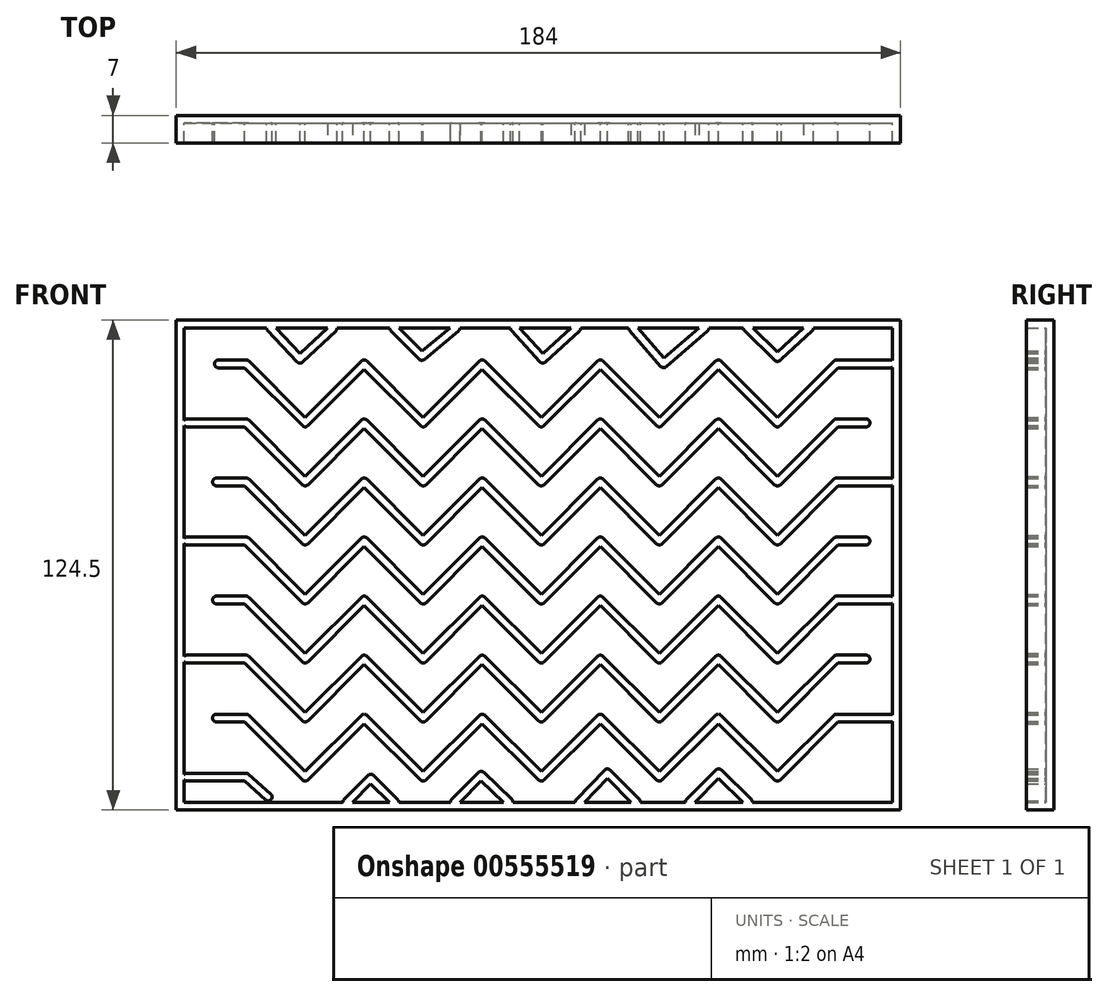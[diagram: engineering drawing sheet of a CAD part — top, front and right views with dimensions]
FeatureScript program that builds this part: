
annotation { "Feature Type Name" : "Feature", "Feature Type Description" : "" }
export const myFeature = defineFeature(function(context is Context, id is Id, definition is map)
    precondition{}
    {
        {
            var Q0;
            Q0=qCreatedBy(makeId("Front.planeOp"),FACE);
            var sketch = newSketch(context, id + "F0", { "sketchPlane" : qUnion([Q0])});
            skLineSegment(sketch, "E0.bottom", {"start": v(-97.27, 65.7) * mm, "end": v(86.73, 65.7) * mm});
            skLineSegment(sketch, "E0.top", {"start": v(-97.27, -58.8) * mm, "end": v(86.73, -58.8) * mm});
            skLineSegment(sketch, "E0.left", {"start": v(-97.27, 65.7) * mm, "end": v(-97.27, -58.8) * mm});
            skLineSegment(sketch, "E0.right", {"start": v(86.73, 65.7) * mm, "end": v(86.73, -58.8) * mm});
            skSolve(sketch);
        }
        {
            var Q0;
            Q0=makeQuery(id+"F0.imprint","IMPRINT",FACE,{"disambiguationData":[TD([[makeQuery(id+"F0.imprint","IMPRINT",EDGE,{"derivedFrom":sQuery(id+"F0.wireOp",EDGE,"E0.bottom")}),-1.0]])]});
            extrude(context, id + "F1", {"entities" : qUnion([Q0]), "depth" : 7 * mm, "offsetDistance" : 25 * mm});
        }
        {
            var Q0;
            Q0=makeQuery(id+"F1.opExtrude","CAP_FACE",FACE,{"disambiguationData":[OSD([sQuery(id+"F0.wireOp",EDGE,"E0.bottom"),sQuery(id+"F0.wireOp",EDGE,"E0.top"),sQuery(id+"F0.wireOp",EDGE,"E0.left"),sQuery(id+"F0.wireOp",EDGE,"E0.right")])],"isStart":false});
            shell(context, id + "F2", {"entities" : qUnion([Q0]), "thickness" : 2 * mm});
        }
        {
            var Q0;
            Q0=makeQuery(id+"F2.opShell","OFFSET_FACE",FACE,{"disambiguationData":[OSD([sQuery(id+"F0.wireOp",EDGE,"E0.bottom"),sQuery(id+"F0.wireOp",EDGE,"E0.top"),sQuery(id+"F0.wireOp",EDGE,"E0.left"),sQuery(id+"F0.wireOp",EDGE,"E0.right")])]});
            var sketch = newSketch(context, id + "F3", { "sketchPlane" : qUnion([Q0])});
            skLineSegment(sketch, "E1", {"start": v(-94.52, 54.57) * mm, "end": v(-94.52, 69.57) * mm, "construction": true});
            skLineSegment(sketch, "E2", {"start": v(-94.52, 39.57) * mm, "end": v(-94.52, 54.57) * mm, "construction": true});
            skLineSegment(sketch, "E3", {"start": v(-94.52, 24.57) * mm, "end": v(-94.52, 39.57) * mm, "construction": true});
            skLineSegment(sketch, "E4", {"start": v(-94.52, 9.57) * mm, "end": v(-94.52, 24.57) * mm, "construction": true});
            skLineSegment(sketch, "E5", {"start": v(-94.52, -5.43) * mm, "end": v(-94.52, 9.57) * mm, "construction": true});
            skLineSegment(sketch, "E6", {"start": v(-94.52, -20.43) * mm, "end": v(-94.52, -5.43) * mm, "construction": true});
            skLineSegment(sketch, "E7", {"start": v(-94.52, -35.43) * mm, "end": v(-94.52, -20.43) * mm, "construction": true});
            skLineSegment(sketch, "E8", {"start": v(-94.52, -50.43) * mm, "end": v(-94.52, -35.43) * mm, "construction": true});
            skLineSegment(sketch, "E9", {"start": v(-94.52, 69.57) * mm, "end": v(111.1, 69.57) * mm, "construction": true});
            skLineSegment(sketch, "E10", {"start": v(-79.52, 54.57) * mm, "end": v(-64.52, 39.57) * mm});
            skLineSegment(sketch, "E11", {"start": v(-64.52, 39.57) * mm, "end": v(-49.52, 54.57) * mm});
            skLineSegment(sketch, "E12", {"start": v(-49.52, 54.57) * mm, "end": v(-34.52, 39.57) * mm});
            skLineSegment(sketch, "E13", {"start": v(-34.52, 39.57) * mm, "end": v(-19.52, 54.57) * mm});
            skLineSegment(sketch, "E14", {"start": v(-19.52, 54.57) * mm, "end": v(-4.52, 39.57) * mm});
            skLineSegment(sketch, "E15", {"start": v(-4.52, 39.57) * mm, "end": v(10.48, 54.57) * mm});
            skLineSegment(sketch, "E16", {"start": v(10.48, 54.57) * mm, "end": v(25.48, 39.57) * mm});
            skLineSegment(sketch, "E17", {"start": v(25.48, 39.57) * mm, "end": v(40.48, 54.57) * mm});
            skLineSegment(sketch, "E18", {"start": v(40.48, 54.57) * mm, "end": v(55.48, 39.57) * mm});
            skLineSegment(sketch, "E19", {"start": v(55.48, 39.57) * mm, "end": v(70.48, 54.57) * mm});
            skLineSegment(sketch, "E20", {"start": v(70.48, 54.57) * mm, "end": v(84.23, 54.57) * mm});
            skLineSegment(sketch, "E21", {"start": v(-79.52, 39.57) * mm, "end": v(-64.52, 24.57) * mm});
            skLineSegment(sketch, "E22", {"start": v(-64.52, 24.57) * mm, "end": v(-49.52, 39.57) * mm});
            skLineSegment(sketch, "E23", {"start": v(-49.52, 39.57) * mm, "end": v(-34.52, 24.57) * mm});
            skLineSegment(sketch, "E24", {"start": v(-34.52, 24.57) * mm, "end": v(-19.52, 39.57) * mm});
            skLineSegment(sketch, "E25", {"start": v(-19.52, 39.57) * mm, "end": v(-4.52, 24.57) * mm});
            skLineSegment(sketch, "E26", {"start": v(-4.52, 24.57) * mm, "end": v(10.48, 39.57) * mm});
            skLineSegment(sketch, "E27", {"start": v(10.48, 39.57) * mm, "end": v(25.48, 24.57) * mm});
            skLineSegment(sketch, "E28", {"start": v(25.48, 24.57) * mm, "end": v(40.48, 39.57) * mm});
            skLineSegment(sketch, "E29", {"start": v(40.48, 39.57) * mm, "end": v(55.48, 24.57) * mm});
            skLineSegment(sketch, "E30", {"start": v(55.48, 24.57) * mm, "end": v(70.48, 39.57) * mm});
            skLineSegment(sketch, "E31", {"start": v(-79.52, 39.57) * mm, "end": v(-94.52, 39.57) * mm});
            skLineSegment(sketch, "E32", {"start": v(-79.52, 24.57) * mm, "end": v(-64.52, 9.57) * mm});
            skLineSegment(sketch, "E33", {"start": v(-64.52, 9.57) * mm, "end": v(-49.52, 24.57) * mm});
            skLineSegment(sketch, "E34", {"start": v(-49.52, 24.57) * mm, "end": v(-34.52, 9.57) * mm});
            skLineSegment(sketch, "E35", {"start": v(-34.52, 9.57) * mm, "end": v(-19.52, 24.57) * mm});
            skLineSegment(sketch, "E36", {"start": v(-19.52, 24.57) * mm, "end": v(-4.52, 9.57) * mm});
            skLineSegment(sketch, "E37", {"start": v(-4.52, 9.57) * mm, "end": v(10.48, 24.57) * mm});
            skLineSegment(sketch, "E38", {"start": v(10.48, 24.57) * mm, "end": v(25.48, 9.57) * mm});
            skLineSegment(sketch, "E39", {"start": v(25.48, 9.57) * mm, "end": v(40.48, 24.57) * mm});
            skLineSegment(sketch, "E40", {"start": v(40.48, 24.57) * mm, "end": v(55.48, 9.57) * mm});
            skLineSegment(sketch, "E41", {"start": v(55.48, 9.57) * mm, "end": v(70.48, 24.57) * mm});
            skLineSegment(sketch, "E42", {"start": v(70.48, 24.57) * mm, "end": v(84.23, 24.57) * mm});
            skLineSegment(sketch, "E43", {"start": v(-79.52, 9.57) * mm, "end": v(-64.52, -5.43) * mm});
            skLineSegment(sketch, "E44", {"start": v(-64.52, -5.43) * mm, "end": v(-49.52, 9.57) * mm});
            skLineSegment(sketch, "E45", {"start": v(-49.52, 9.57) * mm, "end": v(-34.52, -5.43) * mm});
            skLineSegment(sketch, "E46", {"start": v(-34.52, -5.43) * mm, "end": v(-19.52, 9.57) * mm});
            skLineSegment(sketch, "E47", {"start": v(-19.52, 9.57) * mm, "end": v(-4.52, -5.43) * mm});
            skLineSegment(sketch, "E48", {"start": v(-4.52, -5.43) * mm, "end": v(10.48, 9.57) * mm});
            skLineSegment(sketch, "E49", {"start": v(10.48, 9.57) * mm, "end": v(25.48, -5.43) * mm});
            skLineSegment(sketch, "E50", {"start": v(25.48, -5.43) * mm, "end": v(40.48, 9.57) * mm});
            skLineSegment(sketch, "E51", {"start": v(40.48, 9.57) * mm, "end": v(55.48, -5.43) * mm});
            skLineSegment(sketch, "E52", {"start": v(55.48, -5.43) * mm, "end": v(70.48, 9.57) * mm});
            skLineSegment(sketch, "E53", {"start": v(-79.52, 9.57) * mm, "end": v(-94.52, 9.57) * mm});
            skLineSegment(sketch, "E54", {"start": v(-79.52, -5.43) * mm, "end": v(-64.52, -20.43) * mm});
            skLineSegment(sketch, "E55", {"start": v(-64.52, -20.43) * mm, "end": v(-49.52, -5.43) * mm});
            skLineSegment(sketch, "E56", {"start": v(-49.52, -5.43) * mm, "end": v(-34.52, -20.43) * mm});
            skLineSegment(sketch, "E57", {"start": v(-34.52, -20.43) * mm, "end": v(-19.52, -5.43) * mm});
            skLineSegment(sketch, "E58", {"start": v(-19.52, -5.43) * mm, "end": v(-4.52, -20.43) * mm});
            skLineSegment(sketch, "E59", {"start": v(-4.52, -20.43) * mm, "end": v(10.48, -5.43) * mm});
            skLineSegment(sketch, "E60", {"start": v(10.48, -5.43) * mm, "end": v(25.48, -20.43) * mm});
            skLineSegment(sketch, "E61", {"start": v(25.48, -20.43) * mm, "end": v(40.48, -5.43) * mm});
            skLineSegment(sketch, "E62", {"start": v(40.48, -5.43) * mm, "end": v(55.48, -20.43) * mm});
            skLineSegment(sketch, "E63", {"start": v(55.48, -20.43) * mm, "end": v(70.48, -5.43) * mm});
            skLineSegment(sketch, "E64", {"start": v(70.48, -5.43) * mm, "end": v(84.23, -5.43) * mm});
            skLineSegment(sketch, "E65", {"start": v(-79.52, -20.43) * mm, "end": v(-64.52, -35.43) * mm});
            skLineSegment(sketch, "E66", {"start": v(-64.52, -35.43) * mm, "end": v(-49.52, -20.43) * mm});
            skLineSegment(sketch, "E67", {"start": v(-49.52, -20.43) * mm, "end": v(-34.52, -35.43) * mm});
            skLineSegment(sketch, "E68", {"start": v(-34.52, -35.43) * mm, "end": v(-19.52, -20.43) * mm});
            skLineSegment(sketch, "E69", {"start": v(-19.52, -20.43) * mm, "end": v(-4.52, -35.43) * mm});
            skLineSegment(sketch, "E70", {"start": v(-4.52, -35.43) * mm, "end": v(10.48, -20.43) * mm});
            skLineSegment(sketch, "E71", {"start": v(10.48, -20.43) * mm, "end": v(25.48, -35.43) * mm});
            skLineSegment(sketch, "E72", {"start": v(25.48, -35.43) * mm, "end": v(40.48, -20.43) * mm});
            skLineSegment(sketch, "E73", {"start": v(40.48, -20.43) * mm, "end": v(55.48, -35.43) * mm});
            skLineSegment(sketch, "E74", {"start": v(55.48, -35.43) * mm, "end": v(70.48, -20.43) * mm});
            skLineSegment(sketch, "E75", {"start": v(-79.52, -20.43) * mm, "end": v(-94.52, -20.43) * mm});
            skLineSegment(sketch, "E76", {"start": v(-79.52, -35.43) * mm, "end": v(-64.52, -50.43) * mm});
            skLineSegment(sketch, "E77", {"start": v(-64.52, -50.43) * mm, "end": v(-49.52, -35.43) * mm});
            skLineSegment(sketch, "E78", {"start": v(-49.52, -35.43) * mm, "end": v(-34.52, -50.43) * mm});
            skLineSegment(sketch, "E79", {"start": v(-34.52, -50.43) * mm, "end": v(-19.52, -35.43) * mm});
            skLineSegment(sketch, "E80", {"start": v(-19.52, -35.43) * mm, "end": v(-4.52, -50.43) * mm});
            skLineSegment(sketch, "E81", {"start": v(-4.52, -50.43) * mm, "end": v(10.48, -35.43) * mm});
            skLineSegment(sketch, "E82", {"start": v(10.48, -35.43) * mm, "end": v(25.48, -50.43) * mm});
            skLineSegment(sketch, "E83", {"start": v(25.48, -50.43) * mm, "end": v(40.48, -35.43) * mm});
            skLineSegment(sketch, "E84", {"start": v(40.48, -35.43) * mm, "end": v(55.48, -50.43) * mm});
            skLineSegment(sketch, "E85", {"start": v(55.48, -50.43) * mm, "end": v(70.48, -35.43) * mm});
            skLineSegment(sketch, "E86", {"start": v(70.48, -35.43) * mm, "end": v(84.23, -35.43) * mm});
            skLineSegment(sketch, "E87", {"start": v(-79.52, -50.43) * mm, "end": v(-94.52, -50.43) * mm});
            skLineSegment(sketch, "E88", {"start": v(-79.52, -50.43) * mm, "end": v(-73.91, -55.45) * mm});
            skLineSegment(sketch, "E89", {"start": v(-79.52, 54.57) * mm, "end": v(-86.52, 54.57) * mm});
            skLineSegment(sketch, "E90", {"start": v(-79.52, 24.57) * mm, "end": v(-87.02, 24.57) * mm});
            skPoint(sketch, "E90.endSnap0", {"position": v(-87.02, 39.57) * mm});
            skLineSegment(sketch, "E91", {"start": v(-79.52, -5.43) * mm, "end": v(-87.02, -5.43) * mm});
            skPoint(sketch, "E91.endSnap0", {"position": v(-87.02, 9.57) * mm});
            skLineSegment(sketch, "E92", {"start": v(-79.52, -35.43) * mm, "end": v(-87.02, -35.43) * mm});
            skLineSegment(sketch, "E93", {"start": v(70.48, 39.57) * mm, "end": v(77.98, 39.57) * mm});
            skLineSegment(sketch, "E94", {"start": v(70.48, 9.57) * mm, "end": v(77.98, 9.57) * mm});
            skLineSegment(sketch, "E95", {"start": v(70.48, -20.43) * mm, "end": v(77.98, -20.43) * mm});
            skArc(sketch, "E96.0.startCap", {"start": v(-79.52, -49.43) * mm, "mid": v(-78.52, -50.43) * mm, "end": v(-79.52, -51.43) * mm});
            skArc(sketch, "E96.0.endCap", {"start": v(-94.52, -51.43) * mm, "mid": v(-95.52, -50.43) * mm, "end": v(-94.52, -49.43) * mm});
            skLineSegment(sketch, "E96.0.left", {"start": v(-79.52, -51.43) * mm, "end": v(-94.52, -51.43) * mm});
            skLineSegment(sketch, "E96.0.right", {"start": v(-79.52, -49.43) * mm, "end": v(-94.52, -49.43) * mm});
            skArc(sketch, "E96.1.startCap", {"start": v(-50.23, 38.86) * mm, "mid": v(-50.23, 40.28) * mm, "end": v(-48.82, 40.28) * mm});
            skArc(sketch, "E96.1.endCap", {"start": v(-33.82, 25.28) * mm, "mid": v(-33.82, 23.86) * mm, "end": v(-35.23, 23.86) * mm});
            skLineSegment(sketch, "E96.1.left", {"start": v(-48.82, 40.28) * mm, "end": v(-33.82, 25.28) * mm});
            skLineSegment(sketch, "E96.1.right", {"start": v(-50.23, 38.86) * mm, "end": v(-35.23, 23.86) * mm});
            skArc(sketch, "E96.2.startCap", {"start": v(9.77, -21.14) * mm, "mid": v(9.77, -19.72) * mm, "end": v(11.18, -19.72) * mm});
            skArc(sketch, "E96.2.endCap", {"start": v(26.18, -34.72) * mm, "mid": v(26.18, -36.14) * mm, "end": v(24.77, -36.14) * mm});
            skLineSegment(sketch, "E96.2.left", {"start": v(11.18, -19.72) * mm, "end": v(26.18, -34.72) * mm});
            skLineSegment(sketch, "E96.2.right", {"start": v(9.77, -21.14) * mm, "end": v(24.77, -36.14) * mm});
            skArc(sketch, "E96.3.startCap", {"start": v(-63.82, -21.14) * mm, "mid": v(-65.23, -21.14) * mm, "end": v(-65.23, -19.72) * mm});
            skArc(sketch, "E96.3.endCap", {"start": v(-50.23, -4.72) * mm, "mid": v(-48.82, -4.72) * mm, "end": v(-48.82, -6.14) * mm});
            skLineSegment(sketch, "E96.3.left", {"start": v(-65.23, -19.72) * mm, "end": v(-50.23, -4.72) * mm});
            skLineSegment(sketch, "E96.3.right", {"start": v(-63.82, -21.14) * mm, "end": v(-48.82, -6.14) * mm});
            skArc(sketch, "E96.4.startCap", {"start": v(26.18, 8.86) * mm, "mid": v(24.77, 8.86) * mm, "end": v(24.77, 10.28) * mm});
            skArc(sketch, "E96.4.endCap", {"start": v(39.77, 25.28) * mm, "mid": v(41.18, 25.28) * mm, "end": v(41.18, 23.86) * mm});
            skLineSegment(sketch, "E96.4.left", {"start": v(24.77, 10.28) * mm, "end": v(39.77, 25.28) * mm});
            skLineSegment(sketch, "E96.4.right", {"start": v(26.18, 8.86) * mm, "end": v(41.18, 23.86) * mm});
            skArc(sketch, "E96.5.startCap", {"start": v(-20.23, -6.14) * mm, "mid": v(-20.23, -4.72) * mm, "end": v(-18.82, -4.72) * mm});
            skArc(sketch, "E96.5.endCap", {"start": v(-3.82, -19.72) * mm, "mid": v(-3.82, -21.14) * mm, "end": v(-5.23, -21.14) * mm});
            skLineSegment(sketch, "E96.5.left", {"start": v(-18.82, -4.72) * mm, "end": v(-3.82, -19.72) * mm});
            skLineSegment(sketch, "E96.5.right", {"start": v(-20.23, -6.14) * mm, "end": v(-5.23, -21.14) * mm});
            skArc(sketch, "E96.6.startCap", {"start": v(-3.82, 23.86) * mm, "mid": v(-5.23, 23.86) * mm, "end": v(-5.23, 25.28) * mm});
            skArc(sketch, "E96.6.endCap", {"start": v(9.77, 40.28) * mm, "mid": v(11.18, 40.28) * mm, "end": v(11.18, 38.86) * mm});
            skLineSegment(sketch, "E96.6.left", {"start": v(-5.23, 25.28) * mm, "end": v(9.77, 40.28) * mm});
            skLineSegment(sketch, "E96.6.right", {"start": v(-3.82, 23.86) * mm, "end": v(11.18, 38.86) * mm});
            skArc(sketch, "E96.7.startCap", {"start": v(70.48, 23.57) * mm, "mid": v(69.48, 24.57) * mm, "end": v(70.48, 25.57) * mm});
            skArc(sketch, "E96.7.endCap", {"start": v(84.23, 25.57) * mm, "mid": v(85.23, 24.57) * mm, "end": v(84.23, 23.57) * mm});
            skLineSegment(sketch, "E96.7.left", {"start": v(70.48, 25.57) * mm, "end": v(84.23, 25.57) * mm});
            skLineSegment(sketch, "E96.7.right", {"start": v(70.48, 23.57) * mm, "end": v(84.23, 23.57) * mm});
            skArc(sketch, "E96.8.startCap", {"start": v(-79.52, 25.57) * mm, "mid": v(-78.52, 24.57) * mm, "end": v(-79.52, 23.57) * mm});
            skArc(sketch, "E96.8.endCap", {"start": v(-87.02, 23.57) * mm, "mid": v(-88.02, 24.57) * mm, "end": v(-87.02, 25.57) * mm});
            skLineSegment(sketch, "E96.8.left", {"start": v(-79.52, 23.57) * mm, "end": v(-87.02, 23.57) * mm});
            skLineSegment(sketch, "E96.8.right", {"start": v(-79.52, 25.57) * mm, "end": v(-87.02, 25.57) * mm});
            skArc(sketch, "E96.9.startCap", {"start": v(39.77, 23.86) * mm, "mid": v(39.77, 25.28) * mm, "end": v(41.18, 25.28) * mm});
            skArc(sketch, "E96.9.endCap", {"start": v(56.18, 10.28) * mm, "mid": v(56.18, 8.86) * mm, "end": v(54.77, 8.86) * mm});
            skLineSegment(sketch, "E96.9.left", {"start": v(41.18, 25.28) * mm, "end": v(56.18, 10.28) * mm});
            skLineSegment(sketch, "E96.9.right", {"start": v(39.77, 23.86) * mm, "end": v(54.77, 8.86) * mm});
            skArc(sketch, "E96.10.startCap", {"start": v(-50.23, -6.14) * mm, "mid": v(-50.23, -4.72) * mm, "end": v(-48.82, -4.72) * mm});
            skArc(sketch, "E96.10.endCap", {"start": v(-33.82, -19.72) * mm, "mid": v(-33.82, -21.14) * mm, "end": v(-35.23, -21.14) * mm});
            skLineSegment(sketch, "E96.10.left", {"start": v(-48.82, -4.72) * mm, "end": v(-33.82, -19.72) * mm});
            skLineSegment(sketch, "E96.10.right", {"start": v(-50.23, -6.14) * mm, "end": v(-35.23, -21.14) * mm});
            skArc(sketch, "E96.11.startCap", {"start": v(-33.82, 23.86) * mm, "mid": v(-35.23, 23.86) * mm, "end": v(-35.23, 25.28) * mm});
            skArc(sketch, "E96.11.endCap", {"start": v(-20.23, 40.28) * mm, "mid": v(-18.82, 40.28) * mm, "end": v(-18.82, 38.86) * mm});
            skLineSegment(sketch, "E96.11.left", {"start": v(-35.23, 25.28) * mm, "end": v(-20.23, 40.28) * mm});
            skLineSegment(sketch, "E96.11.right", {"start": v(-33.82, 23.86) * mm, "end": v(-18.82, 38.86) * mm});
            skArc(sketch, "E96.12.startCap", {"start": v(-80.19, -51.17) * mm, "mid": v(-80.27, -49.76) * mm, "end": v(-78.86, -49.68) * mm});
            skArc(sketch, "E96.12.endCap", {"start": v(-73.25, -54.7) * mm, "mid": v(-73.17, -56.12) * mm, "end": v(-74.58, -56.2) * mm});
            skLineSegment(sketch, "E96.12.left", {"start": v(-78.86, -49.68) * mm, "end": v(-73.25, -54.7) * mm});
            skLineSegment(sketch, "E96.12.right", {"start": v(-80.19, -51.17) * mm, "end": v(-74.58, -56.2) * mm});
            skArc(sketch, "E96.13.startCap", {"start": v(26.18, -36.14) * mm, "mid": v(24.77, -36.14) * mm, "end": v(24.77, -34.72) * mm});
            skArc(sketch, "E96.13.endCap", {"start": v(39.77, -19.72) * mm, "mid": v(41.18, -19.72) * mm, "end": v(41.18, -21.14) * mm});
            skLineSegment(sketch, "E96.13.left", {"start": v(24.77, -34.72) * mm, "end": v(39.77, -19.72) * mm});
            skLineSegment(sketch, "E96.13.right", {"start": v(26.18, -36.14) * mm, "end": v(41.18, -21.14) * mm});
            skArc(sketch, "E96.14.startCap", {"start": v(-20.23, 53.86) * mm, "mid": v(-20.23, 55.28) * mm, "end": v(-18.82, 55.28) * mm});
            skArc(sketch, "E96.14.endCap", {"start": v(-3.82, 40.28) * mm, "mid": v(-3.82, 38.86) * mm, "end": v(-5.23, 38.86) * mm});
            skLineSegment(sketch, "E96.14.left", {"start": v(-18.82, 55.28) * mm, "end": v(-3.82, 40.28) * mm});
            skLineSegment(sketch, "E96.14.right", {"start": v(-20.23, 53.86) * mm, "end": v(-5.23, 38.86) * mm});
            skArc(sketch, "E96.15.startCap", {"start": v(39.77, 53.86) * mm, "mid": v(39.77, 55.28) * mm, "end": v(41.18, 55.28) * mm});
            skArc(sketch, "E96.15.endCap", {"start": v(56.18, 40.28) * mm, "mid": v(56.18, 38.86) * mm, "end": v(54.77, 38.86) * mm});
            skLineSegment(sketch, "E96.15.left", {"start": v(41.18, 55.28) * mm, "end": v(56.18, 40.28) * mm});
            skLineSegment(sketch, "E96.15.right", {"start": v(39.77, 53.86) * mm, "end": v(54.77, 38.86) * mm});
            skArc(sketch, "E96.16.startCap", {"start": v(-80.23, 53.86) * mm, "mid": v(-80.23, 55.28) * mm, "end": v(-78.82, 55.28) * mm});
            skArc(sketch, "E96.16.endCap", {"start": v(-63.82, 40.28) * mm, "mid": v(-63.82, 38.86) * mm, "end": v(-65.23, 38.86) * mm});
            skLineSegment(sketch, "E96.16.left", {"start": v(-78.82, 55.28) * mm, "end": v(-63.82, 40.28) * mm});
            skLineSegment(sketch, "E96.16.right", {"start": v(-80.23, 53.86) * mm, "end": v(-65.23, 38.86) * mm});
            skArc(sketch, "E96.17.startCap", {"start": v(56.18, -36.14) * mm, "mid": v(54.77, -36.14) * mm, "end": v(54.77, -34.72) * mm});
            skArc(sketch, "E96.17.endCap", {"start": v(69.77, -19.72) * mm, "mid": v(71.18, -19.72) * mm, "end": v(71.18, -21.14) * mm});
            skLineSegment(sketch, "E96.17.left", {"start": v(54.77, -34.72) * mm, "end": v(69.77, -19.72) * mm});
            skLineSegment(sketch, "E96.17.right", {"start": v(56.18, -36.14) * mm, "end": v(71.18, -21.14) * mm});
            skArc(sketch, "E96.18.startCap", {"start": v(56.18, -51.14) * mm, "mid": v(54.77, -51.14) * mm, "end": v(54.77, -49.72) * mm});
            skArc(sketch, "E96.18.endCap", {"start": v(69.77, -34.72) * mm, "mid": v(71.18, -34.72) * mm, "end": v(71.18, -36.14) * mm});
            skLineSegment(sketch, "E96.18.left", {"start": v(54.77, -49.72) * mm, "end": v(69.77, -34.72) * mm});
            skLineSegment(sketch, "E96.18.right", {"start": v(56.18, -51.14) * mm, "end": v(71.18, -36.14) * mm});
            skArc(sketch, "E96.19.startCap", {"start": v(-80.23, 38.86) * mm, "mid": v(-80.23, 40.28) * mm, "end": v(-78.82, 40.28) * mm});
            skArc(sketch, "E96.19.endCap", {"start": v(-63.82, 25.28) * mm, "mid": v(-63.82, 23.86) * mm, "end": v(-65.23, 23.86) * mm});
            skLineSegment(sketch, "E96.19.left", {"start": v(-78.82, 40.28) * mm, "end": v(-63.82, 25.28) * mm});
            skLineSegment(sketch, "E96.19.right", {"start": v(-80.23, 38.86) * mm, "end": v(-65.23, 23.86) * mm});
            skArc(sketch, "E96.20.startCap", {"start": v(56.18, 38.86) * mm, "mid": v(54.77, 38.86) * mm, "end": v(54.77, 40.28) * mm});
            skArc(sketch, "E96.20.endCap", {"start": v(69.77, 55.28) * mm, "mid": v(71.18, 55.28) * mm, "end": v(71.18, 53.86) * mm});
            skLineSegment(sketch, "E96.20.left", {"start": v(54.77, 40.28) * mm, "end": v(69.77, 55.28) * mm});
            skLineSegment(sketch, "E96.20.right", {"start": v(56.18, 38.86) * mm, "end": v(71.18, 53.86) * mm});
            skArc(sketch, "E96.21.startCap", {"start": v(-63.82, 38.86) * mm, "mid": v(-65.23, 38.86) * mm, "end": v(-65.23, 40.28) * mm});
            skArc(sketch, "E96.21.endCap", {"start": v(-50.23, 55.28) * mm, "mid": v(-48.82, 55.28) * mm, "end": v(-48.82, 53.86) * mm});
            skLineSegment(sketch, "E96.21.left", {"start": v(-65.23, 40.28) * mm, "end": v(-50.23, 55.28) * mm});
            skLineSegment(sketch, "E96.21.right", {"start": v(-63.82, 38.86) * mm, "end": v(-48.82, 53.86) * mm});
            skArc(sketch, "E96.22.startCap", {"start": v(-50.23, 53.86) * mm, "mid": v(-50.23, 55.28) * mm, "end": v(-48.82, 55.28) * mm});
            skArc(sketch, "E96.22.endCap", {"start": v(-33.82, 40.28) * mm, "mid": v(-33.82, 38.86) * mm, "end": v(-35.23, 38.86) * mm});
            skLineSegment(sketch, "E96.22.left", {"start": v(-48.82, 55.28) * mm, "end": v(-33.82, 40.28) * mm});
            skLineSegment(sketch, "E96.22.right", {"start": v(-50.23, 53.86) * mm, "end": v(-35.23, 38.86) * mm});
            skArc(sketch, "E96.23.startCap", {"start": v(9.77, -36.14) * mm, "mid": v(9.77, -34.72) * mm, "end": v(11.18, -34.72) * mm});
            skArc(sketch, "E96.23.endCap", {"start": v(26.18, -49.72) * mm, "mid": v(26.18, -51.14) * mm, "end": v(24.77, -51.14) * mm});
            skLineSegment(sketch, "E96.23.left", {"start": v(11.18, -34.72) * mm, "end": v(26.18, -49.72) * mm});
            skLineSegment(sketch, "E96.23.right", {"start": v(9.77, -36.14) * mm, "end": v(24.77, -51.14) * mm});
            skArc(sketch, "E96.24.startCap", {"start": v(26.18, -6.14) * mm, "mid": v(24.77, -6.14) * mm, "end": v(24.77, -4.72) * mm});
            skArc(sketch, "E96.24.endCap", {"start": v(39.77, 10.28) * mm, "mid": v(41.18, 10.28) * mm, "end": v(41.18, 8.86) * mm});
            skLineSegment(sketch, "E96.24.left", {"start": v(24.77, -4.72) * mm, "end": v(39.77, 10.28) * mm});
            skLineSegment(sketch, "E96.24.right", {"start": v(26.18, -6.14) * mm, "end": v(41.18, 8.86) * mm});
            skArc(sketch, "E96.25.startCap", {"start": v(-3.82, 38.86) * mm, "mid": v(-5.23, 38.86) * mm, "end": v(-5.23, 40.28) * mm});
            skArc(sketch, "E96.25.endCap", {"start": v(9.77, 55.28) * mm, "mid": v(11.18, 55.28) * mm, "end": v(11.18, 53.86) * mm});
            skLineSegment(sketch, "E96.25.left", {"start": v(-5.23, 40.28) * mm, "end": v(9.77, 55.28) * mm});
            skLineSegment(sketch, "E96.25.right", {"start": v(-3.82, 38.86) * mm, "end": v(11.18, 53.86) * mm});
            skArc(sketch, "E96.26.startCap", {"start": v(26.18, -51.14) * mm, "mid": v(24.77, -51.14) * mm, "end": v(24.77, -49.72) * mm});
            skArc(sketch, "E96.26.endCap", {"start": v(39.77, -34.72) * mm, "mid": v(41.18, -34.72) * mm, "end": v(41.18, -36.14) * mm});
            skLineSegment(sketch, "E96.26.left", {"start": v(24.77, -49.72) * mm, "end": v(39.77, -34.72) * mm});
            skLineSegment(sketch, "E96.26.right", {"start": v(26.18, -51.14) * mm, "end": v(41.18, -36.14) * mm});
            skArc(sketch, "E96.27.startCap", {"start": v(9.77, 53.86) * mm, "mid": v(9.77, 55.28) * mm, "end": v(11.18, 55.28) * mm});
            skArc(sketch, "E96.27.endCap", {"start": v(26.18, 40.28) * mm, "mid": v(26.18, 38.86) * mm, "end": v(24.77, 38.86) * mm});
            skLineSegment(sketch, "E96.27.left", {"start": v(11.18, 55.28) * mm, "end": v(26.18, 40.28) * mm});
            skLineSegment(sketch, "E96.27.right", {"start": v(9.77, 53.86) * mm, "end": v(24.77, 38.86) * mm});
            skArc(sketch, "E96.28.startCap", {"start": v(-50.23, -21.14) * mm, "mid": v(-50.23, -19.72) * mm, "end": v(-48.82, -19.72) * mm});
            skArc(sketch, "E96.28.endCap", {"start": v(-33.82, -34.72) * mm, "mid": v(-33.82, -36.14) * mm, "end": v(-35.23, -36.14) * mm});
            skLineSegment(sketch, "E96.28.left", {"start": v(-48.82, -19.72) * mm, "end": v(-33.82, -34.72) * mm});
            skLineSegment(sketch, "E96.28.right", {"start": v(-50.23, -21.14) * mm, "end": v(-35.23, -36.14) * mm});
            skArc(sketch, "E96.29.startCap", {"start": v(39.77, 8.86) * mm, "mid": v(39.77, 10.28) * mm, "end": v(41.18, 10.28) * mm});
            skArc(sketch, "E96.29.endCap", {"start": v(56.18, -4.72) * mm, "mid": v(56.18, -6.14) * mm, "end": v(54.77, -6.14) * mm});
            skLineSegment(sketch, "E96.29.left", {"start": v(41.18, 10.28) * mm, "end": v(56.18, -4.72) * mm});
            skLineSegment(sketch, "E96.29.right", {"start": v(39.77, 8.86) * mm, "end": v(54.77, -6.14) * mm});
            skArc(sketch, "E96.30.startCap", {"start": v(-33.82, 8.86) * mm, "mid": v(-35.23, 8.86) * mm, "end": v(-35.23, 10.28) * mm});
            skArc(sketch, "E96.30.endCap", {"start": v(-20.23, 25.28) * mm, "mid": v(-18.82, 25.28) * mm, "end": v(-18.82, 23.86) * mm});
            skLineSegment(sketch, "E96.30.left", {"start": v(-35.23, 10.28) * mm, "end": v(-20.23, 25.28) * mm});
            skLineSegment(sketch, "E96.30.right", {"start": v(-33.82, 8.86) * mm, "end": v(-18.82, 23.86) * mm});
            skArc(sketch, "E96.31.startCap", {"start": v(-63.82, -36.14) * mm, "mid": v(-65.23, -36.14) * mm, "end": v(-65.23, -34.72) * mm});
            skArc(sketch, "E96.31.endCap", {"start": v(-50.23, -19.72) * mm, "mid": v(-48.82, -19.72) * mm, "end": v(-48.82, -21.14) * mm});
            skLineSegment(sketch, "E96.31.left", {"start": v(-65.23, -34.72) * mm, "end": v(-50.23, -19.72) * mm});
            skLineSegment(sketch, "E96.31.right", {"start": v(-63.82, -36.14) * mm, "end": v(-48.82, -21.14) * mm});
            skArc(sketch, "E96.32.startCap", {"start": v(-3.82, 8.86) * mm, "mid": v(-5.23, 8.86) * mm, "end": v(-5.23, 10.28) * mm});
            skArc(sketch, "E96.32.endCap", {"start": v(9.77, 25.28) * mm, "mid": v(11.18, 25.28) * mm, "end": v(11.18, 23.86) * mm});
            skLineSegment(sketch, "E96.32.left", {"start": v(-5.23, 10.28) * mm, "end": v(9.77, 25.28) * mm});
            skLineSegment(sketch, "E96.32.right", {"start": v(-3.82, 8.86) * mm, "end": v(11.18, 23.86) * mm});
            skArc(sketch, "E96.33.startCap", {"start": v(-79.52, 10.57) * mm, "mid": v(-78.52, 9.57) * mm, "end": v(-79.52, 8.57) * mm});
            skArc(sketch, "E96.33.endCap", {"start": v(-94.52, 8.57) * mm, "mid": v(-95.52, 9.57) * mm, "end": v(-94.52, 10.57) * mm});
            skLineSegment(sketch, "E96.33.left", {"start": v(-79.52, 8.57) * mm, "end": v(-94.52, 8.57) * mm});
            skLineSegment(sketch, "E96.33.right", {"start": v(-79.52, 10.57) * mm, "end": v(-94.52, 10.57) * mm});
            skArc(sketch, "E96.34.startCap", {"start": v(-33.82, 38.86) * mm, "mid": v(-35.23, 38.86) * mm, "end": v(-35.23, 40.28) * mm});
            skArc(sketch, "E96.34.endCap", {"start": v(-20.23, 55.28) * mm, "mid": v(-18.82, 55.28) * mm, "end": v(-18.82, 53.86) * mm});
            skLineSegment(sketch, "E96.34.left", {"start": v(-35.23, 40.28) * mm, "end": v(-20.23, 55.28) * mm});
            skLineSegment(sketch, "E96.34.right", {"start": v(-33.82, 38.86) * mm, "end": v(-18.82, 53.86) * mm});
            skArc(sketch, "E96.35.startCap", {"start": v(70.48, 53.57) * mm, "mid": v(69.48, 54.57) * mm, "end": v(70.48, 55.57) * mm});
            skArc(sketch, "E96.35.endCap", {"start": v(84.23, 55.57) * mm, "mid": v(85.23, 54.57) * mm, "end": v(84.23, 53.57) * mm});
            skLineSegment(sketch, "E96.35.left", {"start": v(70.48, 55.57) * mm, "end": v(84.23, 55.57) * mm});
            skLineSegment(sketch, "E96.35.right", {"start": v(70.48, 53.57) * mm, "end": v(84.23, 53.57) * mm});
            skArc(sketch, "E96.36.startCap", {"start": v(39.77, -36.14) * mm, "mid": v(39.77, -34.72) * mm, "end": v(41.18, -34.72) * mm});
            skArc(sketch, "E96.36.endCap", {"start": v(56.18, -49.72) * mm, "mid": v(56.18, -51.14) * mm, "end": v(54.77, -51.14) * mm});
            skLineSegment(sketch, "E96.36.left", {"start": v(41.18, -34.72) * mm, "end": v(56.18, -49.72) * mm});
            skLineSegment(sketch, "E96.36.right", {"start": v(39.77, -36.14) * mm, "end": v(54.77, -51.14) * mm});
            skArc(sketch, "E96.37.startCap", {"start": v(-50.23, 23.86) * mm, "mid": v(-50.23, 25.28) * mm, "end": v(-48.82, 25.28) * mm});
            skArc(sketch, "E96.37.endCap", {"start": v(-33.82, 10.28) * mm, "mid": v(-33.82, 8.86) * mm, "end": v(-35.23, 8.86) * mm});
            skLineSegment(sketch, "E96.37.left", {"start": v(-48.82, 25.28) * mm, "end": v(-33.82, 10.28) * mm});
            skLineSegment(sketch, "E96.37.right", {"start": v(-50.23, 23.86) * mm, "end": v(-35.23, 8.86) * mm});
            skArc(sketch, "E96.38.startCap", {"start": v(-63.82, 23.86) * mm, "mid": v(-65.23, 23.86) * mm, "end": v(-65.23, 25.28) * mm});
            skArc(sketch, "E96.38.endCap", {"start": v(-50.23, 40.28) * mm, "mid": v(-48.82, 40.28) * mm, "end": v(-48.82, 38.86) * mm});
            skLineSegment(sketch, "E96.38.left", {"start": v(-65.23, 25.28) * mm, "end": v(-50.23, 40.28) * mm});
            skLineSegment(sketch, "E96.38.right", {"start": v(-63.82, 23.86) * mm, "end": v(-48.82, 38.86) * mm});
            skArc(sketch, "E96.39.startCap", {"start": v(70.48, -36.43) * mm, "mid": v(69.48, -35.43) * mm, "end": v(70.48, -34.43) * mm});
            skArc(sketch, "E96.39.endCap", {"start": v(84.23, -34.43) * mm, "mid": v(85.23, -35.43) * mm, "end": v(84.23, -36.43) * mm});
            skLineSegment(sketch, "E96.39.left", {"start": v(70.48, -34.43) * mm, "end": v(84.23, -34.43) * mm});
            skLineSegment(sketch, "E96.39.right", {"start": v(70.48, -36.43) * mm, "end": v(84.23, -36.43) * mm});
            skArc(sketch, "E96.40.startCap", {"start": v(-3.82, -36.14) * mm, "mid": v(-5.23, -36.14) * mm, "end": v(-5.23, -34.72) * mm});
            skArc(sketch, "E96.40.endCap", {"start": v(9.77, -19.72) * mm, "mid": v(11.18, -19.72) * mm, "end": v(11.18, -21.14) * mm});
            skLineSegment(sketch, "E96.40.left", {"start": v(-5.23, -34.72) * mm, "end": v(9.77, -19.72) * mm});
            skLineSegment(sketch, "E96.40.right", {"start": v(-3.82, -36.14) * mm, "end": v(11.18, -21.14) * mm});
            skArc(sketch, "E96.41.startCap", {"start": v(-33.82, -21.14) * mm, "mid": v(-35.23, -21.14) * mm, "end": v(-35.23, -19.72) * mm});
            skArc(sketch, "E96.41.endCap", {"start": v(-20.23, -4.72) * mm, "mid": v(-18.82, -4.72) * mm, "end": v(-18.82, -6.14) * mm});
            skLineSegment(sketch, "E96.41.left", {"start": v(-35.23, -19.72) * mm, "end": v(-20.23, -4.72) * mm});
            skLineSegment(sketch, "E96.41.right", {"start": v(-33.82, -21.14) * mm, "end": v(-18.82, -6.14) * mm});
            skArc(sketch, "E96.42.startCap", {"start": v(-33.82, -36.14) * mm, "mid": v(-35.23, -36.14) * mm, "end": v(-35.23, -34.72) * mm});
            skArc(sketch, "E96.42.endCap", {"start": v(-20.23, -19.72) * mm, "mid": v(-18.82, -19.72) * mm, "end": v(-18.82, -21.14) * mm});
            skLineSegment(sketch, "E96.42.left", {"start": v(-35.23, -34.72) * mm, "end": v(-20.23, -19.72) * mm});
            skLineSegment(sketch, "E96.42.right", {"start": v(-33.82, -36.14) * mm, "end": v(-18.82, -21.14) * mm});
            skArc(sketch, "E96.43.startCap", {"start": v(56.18, -6.14) * mm, "mid": v(54.77, -6.14) * mm, "end": v(54.77, -4.72) * mm});
            skArc(sketch, "E96.43.endCap", {"start": v(69.77, 10.28) * mm, "mid": v(71.18, 10.28) * mm, "end": v(71.18, 8.86) * mm});
            skLineSegment(sketch, "E96.43.left", {"start": v(54.77, -4.72) * mm, "end": v(69.77, 10.28) * mm});
            skLineSegment(sketch, "E96.43.right", {"start": v(56.18, -6.14) * mm, "end": v(71.18, 8.86) * mm});
            skArc(sketch, "E96.44.startCap", {"start": v(56.18, 8.86) * mm, "mid": v(54.77, 8.86) * mm, "end": v(54.77, 10.28) * mm});
            skArc(sketch, "E96.44.endCap", {"start": v(69.77, 25.28) * mm, "mid": v(71.18, 25.28) * mm, "end": v(71.18, 23.86) * mm});
            skLineSegment(sketch, "E96.44.left", {"start": v(54.77, 10.28) * mm, "end": v(69.77, 25.28) * mm});
            skLineSegment(sketch, "E96.44.right", {"start": v(56.18, 8.86) * mm, "end": v(71.18, 23.86) * mm});
            skArc(sketch, "E96.45.startCap", {"start": v(-20.23, 38.86) * mm, "mid": v(-20.23, 40.28) * mm, "end": v(-18.82, 40.28) * mm});
            skArc(sketch, "E96.45.endCap", {"start": v(-3.82, 25.28) * mm, "mid": v(-3.82, 23.86) * mm, "end": v(-5.23, 23.86) * mm});
            skLineSegment(sketch, "E96.45.left", {"start": v(-18.82, 40.28) * mm, "end": v(-3.82, 25.28) * mm});
            skLineSegment(sketch, "E96.45.right", {"start": v(-20.23, 38.86) * mm, "end": v(-5.23, 23.86) * mm});
            skArc(sketch, "E96.46.startCap", {"start": v(-79.52, 55.57) * mm, "mid": v(-78.52, 54.57) * mm, "end": v(-79.52, 53.57) * mm});
            skArc(sketch, "E96.46.endCap", {"start": v(-86.52, 53.57) * mm, "mid": v(-87.52, 54.57) * mm, "end": v(-86.52, 55.57) * mm});
            skLineSegment(sketch, "E96.46.left", {"start": v(-79.52, 53.57) * mm, "end": v(-86.52, 53.57) * mm});
            skLineSegment(sketch, "E96.46.right", {"start": v(-79.52, 55.57) * mm, "end": v(-86.52, 55.57) * mm});
            skArc(sketch, "E96.47.startCap", {"start": v(39.77, -21.14) * mm, "mid": v(39.77, -19.72) * mm, "end": v(41.18, -19.72) * mm});
            skArc(sketch, "E96.47.endCap", {"start": v(56.18, -34.72) * mm, "mid": v(56.18, -36.14) * mm, "end": v(54.77, -36.14) * mm});
            skLineSegment(sketch, "E96.47.left", {"start": v(41.18, -19.72) * mm, "end": v(56.18, -34.72) * mm});
            skLineSegment(sketch, "E96.47.right", {"start": v(39.77, -21.14) * mm, "end": v(54.77, -36.14) * mm});
            skArc(sketch, "E96.48.startCap", {"start": v(-20.23, 23.86) * mm, "mid": v(-20.23, 25.28) * mm, "end": v(-18.82, 25.28) * mm});
            skArc(sketch, "E96.48.endCap", {"start": v(-3.82, 10.28) * mm, "mid": v(-3.82, 8.86) * mm, "end": v(-5.23, 8.86) * mm});
            skLineSegment(sketch, "E96.48.left", {"start": v(-18.82, 25.28) * mm, "end": v(-3.82, 10.28) * mm});
            skLineSegment(sketch, "E96.48.right", {"start": v(-20.23, 23.86) * mm, "end": v(-5.23, 8.86) * mm});
            skArc(sketch, "E96.49.startCap", {"start": v(-80.23, -6.14) * mm, "mid": v(-80.23, -4.72) * mm, "end": v(-78.82, -4.72) * mm});
            skArc(sketch, "E96.49.endCap", {"start": v(-63.82, -19.72) * mm, "mid": v(-63.82, -21.14) * mm, "end": v(-65.23, -21.14) * mm});
            skLineSegment(sketch, "E96.49.left", {"start": v(-78.82, -4.72) * mm, "end": v(-63.82, -19.72) * mm});
            skLineSegment(sketch, "E96.49.right", {"start": v(-80.23, -6.14) * mm, "end": v(-65.23, -21.14) * mm});
            skArc(sketch, "E96.50.startCap", {"start": v(9.77, 23.86) * mm, "mid": v(9.77, 25.28) * mm, "end": v(11.18, 25.28) * mm});
            skArc(sketch, "E96.50.endCap", {"start": v(26.18, 10.28) * mm, "mid": v(26.18, 8.86) * mm, "end": v(24.77, 8.86) * mm});
            skLineSegment(sketch, "E96.50.left", {"start": v(11.18, 25.28) * mm, "end": v(26.18, 10.28) * mm});
            skLineSegment(sketch, "E96.50.right", {"start": v(9.77, 23.86) * mm, "end": v(24.77, 8.86) * mm});
            skArc(sketch, "E96.51.startCap", {"start": v(26.18, 38.86) * mm, "mid": v(24.77, 38.86) * mm, "end": v(24.77, 40.28) * mm});
            skArc(sketch, "E96.51.endCap", {"start": v(39.77, 55.28) * mm, "mid": v(41.18, 55.28) * mm, "end": v(41.18, 53.86) * mm});
            skLineSegment(sketch, "E96.51.left", {"start": v(24.77, 40.28) * mm, "end": v(39.77, 55.28) * mm});
            skLineSegment(sketch, "E96.51.right", {"start": v(26.18, 38.86) * mm, "end": v(41.18, 53.86) * mm});
            skArc(sketch, "E96.52.startCap", {"start": v(-63.82, 8.86) * mm, "mid": v(-65.23, 8.86) * mm, "end": v(-65.23, 10.28) * mm});
            skArc(sketch, "E96.52.endCap", {"start": v(-50.23, 25.28) * mm, "mid": v(-48.82, 25.28) * mm, "end": v(-48.82, 23.86) * mm});
            skLineSegment(sketch, "E96.52.left", {"start": v(-65.23, 10.28) * mm, "end": v(-50.23, 25.28) * mm});
            skLineSegment(sketch, "E96.52.right", {"start": v(-63.82, 8.86) * mm, "end": v(-48.82, 23.86) * mm});
            skArc(sketch, "E96.53.startCap", {"start": v(9.77, 8.86) * mm, "mid": v(9.77, 10.28) * mm, "end": v(11.18, 10.28) * mm});
            skArc(sketch, "E96.53.endCap", {"start": v(26.18, -4.72) * mm, "mid": v(26.18, -6.14) * mm, "end": v(24.77, -6.14) * mm});
            skLineSegment(sketch, "E96.53.left", {"start": v(11.18, 10.28) * mm, "end": v(26.18, -4.72) * mm});
            skLineSegment(sketch, "E96.53.right", {"start": v(9.77, 8.86) * mm, "end": v(24.77, -6.14) * mm});
            skArc(sketch, "E96.54.startCap", {"start": v(-80.23, -21.14) * mm, "mid": v(-80.23, -19.72) * mm, "end": v(-78.82, -19.72) * mm});
            skArc(sketch, "E96.54.endCap", {"start": v(-63.82, -34.72) * mm, "mid": v(-63.82, -36.14) * mm, "end": v(-65.23, -36.14) * mm});
            skLineSegment(sketch, "E96.54.left", {"start": v(-78.82, -19.72) * mm, "end": v(-63.82, -34.72) * mm});
            skLineSegment(sketch, "E96.54.right", {"start": v(-80.23, -21.14) * mm, "end": v(-65.23, -36.14) * mm});
            skArc(sketch, "E96.55.startCap", {"start": v(-3.82, -51.14) * mm, "mid": v(-5.23, -51.14) * mm, "end": v(-5.23, -49.72) * mm});
            skArc(sketch, "E96.55.endCap", {"start": v(9.77, -34.72) * mm, "mid": v(11.18, -34.72) * mm, "end": v(11.18, -36.14) * mm});
            skLineSegment(sketch, "E96.55.left", {"start": v(-5.23, -49.72) * mm, "end": v(9.77, -34.72) * mm});
            skLineSegment(sketch, "E96.55.right", {"start": v(-3.82, -51.14) * mm, "end": v(11.18, -36.14) * mm});
            skArc(sketch, "E96.56.startCap", {"start": v(-80.23, 23.86) * mm, "mid": v(-80.23, 25.28) * mm, "end": v(-78.82, 25.28) * mm});
            skArc(sketch, "E96.56.endCap", {"start": v(-63.82, 10.28) * mm, "mid": v(-63.82, 8.86) * mm, "end": v(-65.23, 8.86) * mm});
            skLineSegment(sketch, "E96.56.left", {"start": v(-78.82, 25.28) * mm, "end": v(-63.82, 10.28) * mm});
            skLineSegment(sketch, "E96.56.right", {"start": v(-80.23, 23.86) * mm, "end": v(-65.23, 8.86) * mm});
            skArc(sketch, "E96.57.startCap", {"start": v(-3.82, -6.14) * mm, "mid": v(-5.23, -6.14) * mm, "end": v(-5.23, -4.72) * mm});
            skArc(sketch, "E96.57.endCap", {"start": v(9.77, 10.28) * mm, "mid": v(11.18, 10.28) * mm, "end": v(11.18, 8.86) * mm});
            skLineSegment(sketch, "E96.57.left", {"start": v(-5.23, -4.72) * mm, "end": v(9.77, 10.28) * mm});
            skLineSegment(sketch, "E96.57.right", {"start": v(-3.82, -6.14) * mm, "end": v(11.18, 8.86) * mm});
            skArc(sketch, "E96.58.startCap", {"start": v(70.48, -6.43) * mm, "mid": v(69.48, -5.43) * mm, "end": v(70.48, -4.43) * mm});
            skArc(sketch, "E96.58.endCap", {"start": v(84.23, -4.43) * mm, "mid": v(85.23, -5.43) * mm, "end": v(84.23, -6.43) * mm});
            skLineSegment(sketch, "E96.58.left", {"start": v(70.48, -4.43) * mm, "end": v(84.23, -4.43) * mm});
            skLineSegment(sketch, "E96.58.right", {"start": v(70.48, -6.43) * mm, "end": v(84.23, -6.43) * mm});
            skArc(sketch, "E96.59.startCap", {"start": v(-20.23, -36.14) * mm, "mid": v(-20.23, -34.72) * mm, "end": v(-18.82, -34.72) * mm});
            skArc(sketch, "E96.59.endCap", {"start": v(-3.82, -49.72) * mm, "mid": v(-3.82, -51.14) * mm, "end": v(-5.23, -51.14) * mm});
            skLineSegment(sketch, "E96.59.left", {"start": v(-18.82, -34.72) * mm, "end": v(-3.82, -49.72) * mm});
            skLineSegment(sketch, "E96.59.right", {"start": v(-20.23, -36.14) * mm, "end": v(-5.23, -51.14) * mm});
            skArc(sketch, "E96.60.startCap", {"start": v(70.48, -21.43) * mm, "mid": v(69.48, -20.43) * mm, "end": v(70.48, -19.43) * mm});
            skArc(sketch, "E96.60.endCap", {"start": v(77.98, -19.43) * mm, "mid": v(78.98, -20.43) * mm, "end": v(77.98, -21.43) * mm});
            skLineSegment(sketch, "E96.60.left", {"start": v(70.48, -19.43) * mm, "end": v(77.98, -19.43) * mm});
            skLineSegment(sketch, "E96.60.right", {"start": v(70.48, -21.43) * mm, "end": v(77.98, -21.43) * mm});
            skArc(sketch, "E96.61.startCap", {"start": v(-79.52, 40.57) * mm, "mid": v(-78.52, 39.57) * mm, "end": v(-79.52, 38.57) * mm});
            skArc(sketch, "E96.61.endCap", {"start": v(-94.52, 38.57) * mm, "mid": v(-95.52, 39.57) * mm, "end": v(-94.52, 40.57) * mm});
            skLineSegment(sketch, "E96.61.left", {"start": v(-79.52, 38.57) * mm, "end": v(-94.52, 38.57) * mm});
            skLineSegment(sketch, "E96.61.right", {"start": v(-79.52, 40.57) * mm, "end": v(-94.52, 40.57) * mm});
            skArc(sketch, "E96.62.startCap", {"start": v(-20.23, 8.86) * mm, "mid": v(-20.23, 10.28) * mm, "end": v(-18.82, 10.28) * mm});
            skArc(sketch, "E96.62.endCap", {"start": v(-3.82, -4.72) * mm, "mid": v(-3.82, -6.14) * mm, "end": v(-5.23, -6.14) * mm});
            skLineSegment(sketch, "E96.62.left", {"start": v(-18.82, 10.28) * mm, "end": v(-3.82, -4.72) * mm});
            skLineSegment(sketch, "E96.62.right", {"start": v(-20.23, 8.86) * mm, "end": v(-5.23, -6.14) * mm});
            skArc(sketch, "E96.63.startCap", {"start": v(56.18, -21.14) * mm, "mid": v(54.77, -21.14) * mm, "end": v(54.77, -19.72) * mm});
            skArc(sketch, "E96.63.endCap", {"start": v(69.77, -4.72) * mm, "mid": v(71.18, -4.72) * mm, "end": v(71.18, -6.14) * mm});
            skLineSegment(sketch, "E96.63.left", {"start": v(54.77, -19.72) * mm, "end": v(69.77, -4.72) * mm});
            skLineSegment(sketch, "E96.63.right", {"start": v(56.18, -21.14) * mm, "end": v(71.18, -6.14) * mm});
            skArc(sketch, "E96.64.startCap", {"start": v(-33.82, -51.14) * mm, "mid": v(-35.23, -51.14) * mm, "end": v(-35.23, -49.72) * mm});
            skArc(sketch, "E96.64.endCap", {"start": v(-20.23, -34.72) * mm, "mid": v(-18.82, -34.72) * mm, "end": v(-18.82, -36.14) * mm});
            skLineSegment(sketch, "E96.64.left", {"start": v(-35.23, -49.72) * mm, "end": v(-20.23, -34.72) * mm});
            skLineSegment(sketch, "E96.64.right", {"start": v(-33.82, -51.14) * mm, "end": v(-18.82, -36.14) * mm});
            skArc(sketch, "E96.65.startCap", {"start": v(-63.82, -51.14) * mm, "mid": v(-65.23, -51.14) * mm, "end": v(-65.23, -49.72) * mm});
            skArc(sketch, "E96.65.endCap", {"start": v(-50.23, -34.72) * mm, "mid": v(-48.82, -34.72) * mm, "end": v(-48.82, -36.14) * mm});
            skLineSegment(sketch, "E96.65.left", {"start": v(-65.23, -49.72) * mm, "end": v(-50.23, -34.72) * mm});
            skLineSegment(sketch, "E96.65.right", {"start": v(-63.82, -51.14) * mm, "end": v(-48.82, -36.14) * mm});
            skArc(sketch, "E96.66.startCap", {"start": v(70.48, 38.57) * mm, "mid": v(69.48, 39.57) * mm, "end": v(70.48, 40.57) * mm});
            skArc(sketch, "E96.66.endCap", {"start": v(77.98, 40.57) * mm, "mid": v(78.98, 39.57) * mm, "end": v(77.98, 38.57) * mm});
            skLineSegment(sketch, "E96.66.left", {"start": v(70.48, 40.57) * mm, "end": v(77.98, 40.57) * mm});
            skLineSegment(sketch, "E96.66.right", {"start": v(70.48, 38.57) * mm, "end": v(77.98, 38.57) * mm});
            skArc(sketch, "E96.67.startCap", {"start": v(39.77, 38.86) * mm, "mid": v(39.77, 40.28) * mm, "end": v(41.18, 40.28) * mm});
            skArc(sketch, "E96.67.endCap", {"start": v(56.18, 25.28) * mm, "mid": v(56.18, 23.86) * mm, "end": v(54.77, 23.86) * mm});
            skLineSegment(sketch, "E96.67.left", {"start": v(41.18, 40.28) * mm, "end": v(56.18, 25.28) * mm});
            skLineSegment(sketch, "E96.67.right", {"start": v(39.77, 38.86) * mm, "end": v(54.77, 23.86) * mm});
            skArc(sketch, "E96.68.startCap", {"start": v(-50.23, 8.86) * mm, "mid": v(-50.23, 10.28) * mm, "end": v(-48.82, 10.28) * mm});
            skArc(sketch, "E96.68.endCap", {"start": v(-33.82, -4.72) * mm, "mid": v(-33.82, -6.14) * mm, "end": v(-35.23, -6.14) * mm});
            skLineSegment(sketch, "E96.68.left", {"start": v(-48.82, 10.28) * mm, "end": v(-33.82, -4.72) * mm});
            skLineSegment(sketch, "E96.68.right", {"start": v(-50.23, 8.86) * mm, "end": v(-35.23, -6.14) * mm});
            skArc(sketch, "E96.69.startCap", {"start": v(26.18, -21.14) * mm, "mid": v(24.77, -21.14) * mm, "end": v(24.77, -19.72) * mm});
            skArc(sketch, "E96.69.endCap", {"start": v(39.77, -4.72) * mm, "mid": v(41.18, -4.72) * mm, "end": v(41.18, -6.14) * mm});
            skLineSegment(sketch, "E96.69.left", {"start": v(24.77, -19.72) * mm, "end": v(39.77, -4.72) * mm});
            skLineSegment(sketch, "E96.69.right", {"start": v(26.18, -21.14) * mm, "end": v(41.18, -6.14) * mm});
            skArc(sketch, "E96.70.startCap", {"start": v(70.48, 8.57) * mm, "mid": v(69.48, 9.57) * mm, "end": v(70.48, 10.57) * mm});
            skArc(sketch, "E96.70.endCap", {"start": v(77.98, 10.57) * mm, "mid": v(78.98, 9.57) * mm, "end": v(77.98, 8.57) * mm});
            skLineSegment(sketch, "E96.70.left", {"start": v(70.48, 10.57) * mm, "end": v(77.98, 10.57) * mm});
            skLineSegment(sketch, "E96.70.right", {"start": v(70.48, 8.57) * mm, "end": v(77.98, 8.57) * mm});
            skArc(sketch, "E96.71.startCap", {"start": v(56.18, 23.86) * mm, "mid": v(54.77, 23.86) * mm, "end": v(54.77, 25.28) * mm});
            skArc(sketch, "E96.71.endCap", {"start": v(69.77, 40.28) * mm, "mid": v(71.18, 40.28) * mm, "end": v(71.18, 38.86) * mm});
            skLineSegment(sketch, "E96.71.left", {"start": v(54.77, 25.28) * mm, "end": v(69.77, 40.28) * mm});
            skLineSegment(sketch, "E96.71.right", {"start": v(56.18, 23.86) * mm, "end": v(71.18, 38.86) * mm});
            skArc(sketch, "E96.72.startCap", {"start": v(-33.82, -6.14) * mm, "mid": v(-35.23, -6.14) * mm, "end": v(-35.23, -4.72) * mm});
            skArc(sketch, "E96.72.endCap", {"start": v(-20.23, 10.28) * mm, "mid": v(-18.82, 10.28) * mm, "end": v(-18.82, 8.86) * mm});
            skLineSegment(sketch, "E96.72.left", {"start": v(-35.23, -4.72) * mm, "end": v(-20.23, 10.28) * mm});
            skLineSegment(sketch, "E96.72.right", {"start": v(-33.82, -6.14) * mm, "end": v(-18.82, 8.86) * mm});
            skArc(sketch, "E96.73.startCap", {"start": v(39.77, -6.14) * mm, "mid": v(39.77, -4.72) * mm, "end": v(41.18, -4.72) * mm});
            skArc(sketch, "E96.73.endCap", {"start": v(56.18, -19.72) * mm, "mid": v(56.18, -21.14) * mm, "end": v(54.77, -21.14) * mm});
            skLineSegment(sketch, "E96.73.left", {"start": v(41.18, -4.72) * mm, "end": v(56.18, -19.72) * mm});
            skLineSegment(sketch, "E96.73.right", {"start": v(39.77, -6.14) * mm, "end": v(54.77, -21.14) * mm});
            skArc(sketch, "E96.74.startCap", {"start": v(-50.23, -36.14) * mm, "mid": v(-50.23, -34.72) * mm, "end": v(-48.82, -34.72) * mm});
            skArc(sketch, "E96.74.endCap", {"start": v(-33.82, -49.72) * mm, "mid": v(-33.82, -51.14) * mm, "end": v(-35.23, -51.14) * mm});
            skLineSegment(sketch, "E96.74.left", {"start": v(-48.82, -34.72) * mm, "end": v(-33.82, -49.72) * mm});
            skLineSegment(sketch, "E96.74.right", {"start": v(-50.23, -36.14) * mm, "end": v(-35.23, -51.14) * mm});
            skArc(sketch, "E96.75.startCap", {"start": v(-80.23, -36.14) * mm, "mid": v(-80.23, -34.72) * mm, "end": v(-78.82, -34.72) * mm});
            skArc(sketch, "E96.75.endCap", {"start": v(-63.82, -49.72) * mm, "mid": v(-63.82, -51.14) * mm, "end": v(-65.23, -51.14) * mm});
            skLineSegment(sketch, "E96.75.left", {"start": v(-78.82, -34.72) * mm, "end": v(-63.82, -49.72) * mm});
            skLineSegment(sketch, "E96.75.right", {"start": v(-80.23, -36.14) * mm, "end": v(-65.23, -51.14) * mm});
            skArc(sketch, "E96.76.startCap", {"start": v(26.18, 23.86) * mm, "mid": v(24.77, 23.86) * mm, "end": v(24.77, 25.28) * mm});
            skArc(sketch, "E96.76.endCap", {"start": v(39.77, 40.28) * mm, "mid": v(41.18, 40.28) * mm, "end": v(41.18, 38.86) * mm});
            skLineSegment(sketch, "E96.76.left", {"start": v(24.77, 25.28) * mm, "end": v(39.77, 40.28) * mm});
            skLineSegment(sketch, "E96.76.right", {"start": v(26.18, 23.86) * mm, "end": v(41.18, 38.86) * mm});
            skArc(sketch, "E96.77.startCap", {"start": v(-79.52, -34.43) * mm, "mid": v(-78.52, -35.43) * mm, "end": v(-79.52, -36.43) * mm});
            skArc(sketch, "E96.77.endCap", {"start": v(-87.02, -36.43) * mm, "mid": v(-88.02, -35.43) * mm, "end": v(-87.02, -34.43) * mm});
            skLineSegment(sketch, "E96.77.left", {"start": v(-79.52, -36.43) * mm, "end": v(-87.02, -36.43) * mm});
            skLineSegment(sketch, "E96.77.right", {"start": v(-79.52, -34.43) * mm, "end": v(-87.02, -34.43) * mm});
            skArc(sketch, "E96.78.startCap", {"start": v(-63.82, -6.14) * mm, "mid": v(-65.23, -6.14) * mm, "end": v(-65.23, -4.72) * mm});
            skArc(sketch, "E96.78.endCap", {"start": v(-50.23, 10.28) * mm, "mid": v(-48.82, 10.28) * mm, "end": v(-48.82, 8.86) * mm});
            skLineSegment(sketch, "E96.78.left", {"start": v(-65.23, -4.72) * mm, "end": v(-50.23, 10.28) * mm});
            skLineSegment(sketch, "E96.78.right", {"start": v(-63.82, -6.14) * mm, "end": v(-48.82, 8.86) * mm});
            skArc(sketch, "E96.79.startCap", {"start": v(9.77, -6.14) * mm, "mid": v(9.77, -4.72) * mm, "end": v(11.18, -4.72) * mm});
            skArc(sketch, "E96.79.endCap", {"start": v(26.18, -19.72) * mm, "mid": v(26.18, -21.14) * mm, "end": v(24.77, -21.14) * mm});
            skLineSegment(sketch, "E96.79.left", {"start": v(11.18, -4.72) * mm, "end": v(26.18, -19.72) * mm});
            skLineSegment(sketch, "E96.79.right", {"start": v(9.77, -6.14) * mm, "end": v(24.77, -21.14) * mm});
            skArc(sketch, "E96.80.startCap", {"start": v(-79.52, -4.43) * mm, "mid": v(-78.52, -5.43) * mm, "end": v(-79.52, -6.43) * mm});
            skArc(sketch, "E96.80.endCap", {"start": v(-87.02, -6.43) * mm, "mid": v(-88.02, -5.43) * mm, "end": v(-87.02, -4.43) * mm});
            skLineSegment(sketch, "E96.80.left", {"start": v(-79.52, -6.43) * mm, "end": v(-87.02, -6.43) * mm});
            skLineSegment(sketch, "E96.80.right", {"start": v(-79.52, -4.43) * mm, "end": v(-87.02, -4.43) * mm});
            skArc(sketch, "E96.81.startCap", {"start": v(-80.23, 8.86) * mm, "mid": v(-80.23, 10.28) * mm, "end": v(-78.82, 10.28) * mm});
            skArc(sketch, "E96.81.endCap", {"start": v(-63.82, -4.72) * mm, "mid": v(-63.82, -6.14) * mm, "end": v(-65.23, -6.14) * mm});
            skLineSegment(sketch, "E96.81.left", {"start": v(-78.82, 10.28) * mm, "end": v(-63.82, -4.72) * mm});
            skLineSegment(sketch, "E96.81.right", {"start": v(-80.23, 8.86) * mm, "end": v(-65.23, -6.14) * mm});
            skArc(sketch, "E96.82.startCap", {"start": v(9.77, 38.86) * mm, "mid": v(9.77, 40.28) * mm, "end": v(11.18, 40.28) * mm});
            skArc(sketch, "E96.82.endCap", {"start": v(26.18, 25.28) * mm, "mid": v(26.18, 23.86) * mm, "end": v(24.77, 23.86) * mm});
            skLineSegment(sketch, "E96.82.left", {"start": v(11.18, 40.28) * mm, "end": v(26.18, 25.28) * mm});
            skLineSegment(sketch, "E96.82.right", {"start": v(9.77, 38.86) * mm, "end": v(24.77, 23.86) * mm});
            skArc(sketch, "E96.83.startCap", {"start": v(-20.23, -21.14) * mm, "mid": v(-20.23, -19.72) * mm, "end": v(-18.82, -19.72) * mm});
            skArc(sketch, "E96.83.endCap", {"start": v(-3.82, -34.72) * mm, "mid": v(-3.82, -36.14) * mm, "end": v(-5.23, -36.14) * mm});
            skLineSegment(sketch, "E96.83.left", {"start": v(-18.82, -19.72) * mm, "end": v(-3.82, -34.72) * mm});
            skLineSegment(sketch, "E96.83.right", {"start": v(-20.23, -21.14) * mm, "end": v(-5.23, -36.14) * mm});
            skArc(sketch, "E96.84.startCap", {"start": v(-3.82, -21.14) * mm, "mid": v(-5.23, -21.14) * mm, "end": v(-5.23, -19.72) * mm});
            skArc(sketch, "E96.84.endCap", {"start": v(9.77, -4.72) * mm, "mid": v(11.18, -4.72) * mm, "end": v(11.18, -6.14) * mm});
            skLineSegment(sketch, "E96.84.left", {"start": v(-5.23, -19.72) * mm, "end": v(9.77, -4.72) * mm});
            skLineSegment(sketch, "E96.84.right", {"start": v(-3.82, -21.14) * mm, "end": v(11.18, -6.14) * mm});
            skArc(sketch, "E96.85.startCap", {"start": v(-79.52, -19.43) * mm, "mid": v(-78.52, -20.43) * mm, "end": v(-79.52, -21.43) * mm});
            skArc(sketch, "E96.85.endCap", {"start": v(-94.52, -21.43) * mm, "mid": v(-95.52, -20.43) * mm, "end": v(-94.52, -19.43) * mm});
            skLineSegment(sketch, "E96.85.left", {"start": v(-79.52, -21.43) * mm, "end": v(-94.52, -21.43) * mm});
            skLineSegment(sketch, "E96.85.right", {"start": v(-79.52, -19.43) * mm, "end": v(-94.52, -19.43) * mm});
            skLineSegment(sketch, "E97", {"start": v(-73.33, 63.7) * mm, "end": v(-65.83, 55.75) * mm});
            skLineSegment(sketch, "E98", {"start": v(-65.83, 55.75) * mm, "end": v(-57.4, 63.7) * mm});
            skLineSegment(sketch, "E99", {"start": v(-42.05, 63.7) * mm, "end": v(-34.9, 56.46) * mm});
            skLineSegment(sketch, "E100", {"start": v(-34.9, 56.46) * mm, "end": v(-26.2, 63.7) * mm});
            skLineSegment(sketch, "E101", {"start": v(-11.4, 63.7) * mm, "end": v(-4.16, 55.77) * mm});
            skLineSegment(sketch, "E102", {"start": v(-4.16, 55.77) * mm, "end": v(4.52, 63.7) * mm});
            skLineSegment(sketch, "E103", {"start": v(18.67, 63.7) * mm, "end": v(26.57, 54.6) * mm});
            skLineSegment(sketch, "E104", {"start": v(26.57, 54.6) * mm, "end": v(37.07, 63.7) * mm});
            skLineSegment(sketch, "E105", {"start": v(47.77, 63.7) * mm, "end": v(55.5, 56.19) * mm});
            skLineSegment(sketch, "E106", {"start": v(55.42, 56.27) * mm, "end": v(63.62, 63.7) * mm});
            skLineSegment(sketch, "E107", {"start": v(-4.16, 55.77) * mm, "end": v(-4.16, 55.77) * mm});
            skArc(sketch, "E108.0.startCap", {"start": v(-3.49, 55.04) * mm, "mid": v(-4.9, 55.1) * mm, "end": v(-4.84, 56.51) * mm});
            skArc(sketch, "E108.0.endCap", {"start": v(3.85, 64.44) * mm, "mid": v(5.26, 64.38) * mm, "end": v(5.2, 62.96) * mm});
            skLineSegment(sketch, "E108.0.left", {"start": v(-4.84, 56.51) * mm, "end": v(3.85, 64.44) * mm});
            skLineSegment(sketch, "E108.0.right", {"start": v(-3.49, 55.04) * mm, "end": v(5.2, 62.96) * mm});
            skArc(sketch, "E108.1.startCap", {"start": v(-12.15, 63.03) * mm, "mid": v(-12.08, 64.44) * mm, "end": v(-10.67, 64.38) * mm});
            skArc(sketch, "E108.1.endCap", {"start": v(-3.42, 56.45) * mm, "mid": v(-3.49, 55.04) * mm, "end": v(-4.9, 55.1) * mm});
            skLineSegment(sketch, "E108.1.left", {"start": v(-10.67, 64.38) * mm, "end": v(-3.42, 56.45) * mm});
            skLineSegment(sketch, "E108.1.right", {"start": v(-12.15, 63.03) * mm, "end": v(-4.9, 55.1) * mm});
            skArc(sketch, "E108.2.startCap", {"start": v(-34.25, 55.7) * mm, "mid": v(-35.66, 55.82) * mm, "end": v(-35.53, 57.23) * mm});
            skArc(sketch, "E108.2.endCap", {"start": v(-26.84, 64.47) * mm, "mid": v(-25.44, 64.34) * mm, "end": v(-25.56, 62.94) * mm});
            skLineSegment(sketch, "E108.2.left", {"start": v(-35.53, 57.23) * mm, "end": v(-26.84, 64.47) * mm});
            skLineSegment(sketch, "E108.2.right", {"start": v(-34.25, 55.7) * mm, "end": v(-25.56, 62.94) * mm});
            skArc(sketch, "E108.3.startCap", {"start": v(-42.76, 63) * mm, "mid": v(-42.76, 64.41) * mm, "end": v(-41.34, 64.4) * mm});
            skArc(sketch, "E108.3.endCap", {"start": v(-34.18, 57.17) * mm, "mid": v(-34.19, 55.75) * mm, "end": v(-35.6, 55.76) * mm});
            skLineSegment(sketch, "E108.3.left", {"start": v(-41.34, 64.4) * mm, "end": v(-34.18, 57.17) * mm});
            skLineSegment(sketch, "E108.3.right", {"start": v(-42.76, 63) * mm, "end": v(-35.6, 55.76) * mm});
            skArc(sketch, "E108.4.startCap", {"start": v(-65.15, 55.02) * mm, "mid": v(-66.56, 55.06) * mm, "end": v(-66.52, 56.48) * mm});
            skArc(sketch, "E108.4.endCap", {"start": v(-58.08, 64.43) * mm, "mid": v(-56.67, 64.39) * mm, "end": v(-56.7, 62.98) * mm});
            skLineSegment(sketch, "E108.4.left", {"start": v(-66.52, 56.48) * mm, "end": v(-58.08, 64.43) * mm});
            skLineSegment(sketch, "E108.4.right", {"start": v(-65.15, 55.02) * mm, "end": v(-56.7, 62.98) * mm});
            skArc(sketch, "E108.5.startCap", {"start": v(-74.06, 63.02) * mm, "mid": v(-74.02, 64.43) * mm, "end": v(-72.6, 64.39) * mm});
            skArc(sketch, "E108.5.endCap", {"start": v(-65.1, 56.43) * mm, "mid": v(-65.15, 55.02) * mm, "end": v(-66.56, 55.06) * mm});
            skLineSegment(sketch, "E108.5.left", {"start": v(-72.6, 64.39) * mm, "end": v(-65.1, 56.43) * mm});
            skLineSegment(sketch, "E108.5.right", {"start": v(-74.06, 63.02) * mm, "end": v(-66.56, 55.06) * mm});
            skArc(sketch, "E108.6.startCap", {"start": v(56.1, 55.53) * mm, "mid": v(54.68, 55.6) * mm, "end": v(54.75, 57.01) * mm});
            skArc(sketch, "E108.6.endCap", {"start": v(62.95, 64.44) * mm, "mid": v(64.36, 64.38) * mm, "end": v(64.3, 62.96) * mm});
            skLineSegment(sketch, "E108.6.left", {"start": v(54.75, 57.01) * mm, "end": v(62.95, 64.44) * mm});
            skLineSegment(sketch, "E108.6.right", {"start": v(56.1, 55.53) * mm, "end": v(64.3, 62.96) * mm});
            skArc(sketch, "E108.7.startCap", {"start": v(47.07, 62.99) * mm, "mid": v(47.05, 64.4) * mm, "end": v(48.47, 64.42) * mm});
            skArc(sketch, "E108.7.endCap", {"start": v(56.2, 56.9) * mm, "mid": v(56.22, 55.5) * mm, "end": v(54.8, 55.47) * mm});
            skLineSegment(sketch, "E108.7.left", {"start": v(48.47, 64.42) * mm, "end": v(56.2, 56.9) * mm});
            skLineSegment(sketch, "E108.7.right", {"start": v(47.07, 62.99) * mm, "end": v(54.8, 55.47) * mm});
            skArc(sketch, "E108.8.startCap", {"start": v(27.22, 53.84) * mm, "mid": v(25.81, 53.94) * mm, "end": v(25.91, 55.35) * mm});
            skArc(sketch, "E108.8.endCap", {"start": v(36.41, 64.46) * mm, "mid": v(37.83, 64.36) * mm, "end": v(37.72, 62.95) * mm});
            skLineSegment(sketch, "E108.8.left", {"start": v(25.91, 55.35) * mm, "end": v(36.41, 64.46) * mm});
            skLineSegment(sketch, "E108.8.right", {"start": v(27.22, 53.84) * mm, "end": v(37.72, 62.95) * mm});
            skArc(sketch, "E108.9.startCap", {"start": v(17.91, 63.05) * mm, "mid": v(18.01, 64.46) * mm, "end": v(19.42, 64.36) * mm});
            skArc(sketch, "E108.9.endCap", {"start": v(27.32, 55.25) * mm, "mid": v(27.22, 53.84) * mm, "end": v(25.81, 53.94) * mm});
            skLineSegment(sketch, "E108.9.left", {"start": v(19.42, 64.36) * mm, "end": v(27.32, 55.25) * mm});
            skLineSegment(sketch, "E108.9.right", {"start": v(17.91, 63.05) * mm, "end": v(25.81, 53.94) * mm});
            skLineSegment(sketch, "E109", {"start": v(-53.95, -56.8) * mm, "end": v(-47.84, -50.68) * mm});
            skLineSegment(sketch, "E110", {"start": v(-47.84, -50.68) * mm, "end": v(-41.72, -56.8) * mm});
            skLineSegment(sketch, "E111", {"start": v(-26.6, -56.8) * mm, "end": v(-19.79, -49.98) * mm});
            skLineSegment(sketch, "E112", {"start": v(-19.79, -49.98) * mm, "end": v(-12.72, -56.8) * mm});
            skLineSegment(sketch, "E113", {"start": v(5.08, -56.8) * mm, "end": v(12.23, -49.35) * mm});
            skLineSegment(sketch, "E114", {"start": v(12.23, -49.35) * mm, "end": v(19.67, -56.8) * mm});
            skLineSegment(sketch, "E115", {"start": v(33.07, -56.8) * mm, "end": v(40.53, -49.34) * mm});
            skLineSegment(sketch, "E116", {"start": v(40.53, -49.34) * mm, "end": v(48.1, -56.8) * mm});
            skArc(sketch, "E117.0.startCap", {"start": v(5.8, -57.49) * mm, "mid": v(4.38, -57.52) * mm, "end": v(4.36, -56.1) * mm});
            skArc(sketch, "E117.0.endCap", {"start": v(11.5, -48.66) * mm, "mid": v(12.92, -48.63) * mm, "end": v(12.95, -50.05) * mm});
            skLineSegment(sketch, "E117.0.left", {"start": v(4.36, -56.1) * mm, "end": v(11.5, -48.66) * mm});
            skLineSegment(sketch, "E117.0.right", {"start": v(5.8, -57.49) * mm, "end": v(12.95, -50.05) * mm});
            skArc(sketch, "E117.1.startCap", {"start": v(-20.48, -50.7) * mm, "mid": v(-20.5, -49.28) * mm, "end": v(-19.1, -49.26) * mm});
            skArc(sketch, "E117.1.endCap", {"start": v(-12.02, -56.08) * mm, "mid": v(-12, -57.5) * mm, "end": v(-13.41, -57.52) * mm});
            skLineSegment(sketch, "E117.1.left", {"start": v(-19.1, -49.26) * mm, "end": v(-12.02, -56.08) * mm});
            skLineSegment(sketch, "E117.1.right", {"start": v(-20.48, -50.7) * mm, "end": v(-13.41, -57.52) * mm});
            skArc(sketch, "E117.2.startCap", {"start": v(-25.9, -57.5) * mm, "mid": v(-27.31, -57.5) * mm, "end": v(-27.31, -56.09) * mm});
            skArc(sketch, "E117.2.endCap", {"start": v(-20.5, -49.27) * mm, "mid": v(-19.08, -49.27) * mm, "end": v(-19.08, -50.69) * mm});
            skLineSegment(sketch, "E117.2.left", {"start": v(-27.31, -56.09) * mm, "end": v(-20.5, -49.27) * mm});
            skLineSegment(sketch, "E117.2.right", {"start": v(-25.9, -57.5) * mm, "end": v(-19.08, -50.69) * mm});
            skArc(sketch, "E117.3.startCap", {"start": v(-48.54, -51.39) * mm, "mid": v(-48.54, -49.97) * mm, "end": v(-47.13, -49.97) * mm});
            skArc(sketch, "E117.3.endCap", {"start": v(-41.01, -56.09) * mm, "mid": v(-41.01, -57.5) * mm, "end": v(-42.43, -57.5) * mm});
            skLineSegment(sketch, "E117.3.left", {"start": v(-47.13, -49.97) * mm, "end": v(-41.01, -56.09) * mm});
            skLineSegment(sketch, "E117.3.right", {"start": v(-48.54, -51.39) * mm, "end": v(-42.43, -57.5) * mm});
            skArc(sketch, "E117.4.startCap", {"start": v(-53.24, -57.5) * mm, "mid": v(-54.66, -57.5) * mm, "end": v(-54.66, -56.09) * mm});
            skArc(sketch, "E117.4.endCap", {"start": v(-48.54, -49.97) * mm, "mid": v(-47.13, -49.97) * mm, "end": v(-47.13, -51.39) * mm});
            skLineSegment(sketch, "E117.4.left", {"start": v(-54.66, -56.09) * mm, "end": v(-48.54, -49.97) * mm});
            skLineSegment(sketch, "E117.4.right", {"start": v(-53.24, -57.5) * mm, "end": v(-47.13, -51.39) * mm});
            skArc(sketch, "E117.5.startCap", {"start": v(39.83, -50.05) * mm, "mid": v(39.82, -48.64) * mm, "end": v(41.23, -48.63) * mm});
            skArc(sketch, "E117.5.endCap", {"start": v(48.8, -56.08) * mm, "mid": v(48.82, -57.5) * mm, "end": v(47.4, -57.5) * mm});
            skLineSegment(sketch, "E117.5.left", {"start": v(41.23, -48.63) * mm, "end": v(48.8, -56.08) * mm});
            skLineSegment(sketch, "E117.5.right", {"start": v(39.83, -50.05) * mm, "end": v(47.4, -57.5) * mm});
            skArc(sketch, "E117.6.startCap", {"start": v(33.78, -57.5) * mm, "mid": v(32.37, -57.5) * mm, "end": v(32.37, -56.09) * mm});
            skArc(sketch, "E117.6.endCap", {"start": v(39.82, -48.63) * mm, "mid": v(41.24, -48.63) * mm, "end": v(41.24, -50.05) * mm});
            skLineSegment(sketch, "E117.6.left", {"start": v(32.37, -56.09) * mm, "end": v(39.82, -48.63) * mm});
            skLineSegment(sketch, "E117.6.right", {"start": v(33.78, -57.5) * mm, "end": v(41.24, -50.05) * mm});
            skArc(sketch, "E117.7.startCap", {"start": v(11.52, -50.06) * mm, "mid": v(11.52, -48.65) * mm, "end": v(12.94, -48.65) * mm});
            skArc(sketch, "E117.7.endCap", {"start": v(20.38, -56.09) * mm, "mid": v(20.38, -57.5) * mm, "end": v(18.97, -57.5) * mm});
            skLineSegment(sketch, "E117.7.left", {"start": v(12.94, -48.65) * mm, "end": v(20.38, -56.09) * mm});
            skLineSegment(sketch, "E117.7.right", {"start": v(11.52, -50.06) * mm, "end": v(18.97, -57.5) * mm});
            skSolve(sketch);
        }
        {
            var Q0;
            Q0=qSketchRegion(id+"F3",true);
            extrude(context, id + "F4", {"entities" : qUnion([Q0]), "operationType" : NewBodyOperationType.ADD, "depth" : 5 * mm, "offsetDistance" : 25 * mm});
        }
    });
